# Revit family: шаблон семейства 2017
name_source: partatom
category: Датчики
revit_build: Autodesk Revit 2017 (Build: 20170118_1100(x64)
units: mm (PartAtom-declared; Revit-internal decimal feet)

## family parameters
Всегда вертикально = Нет
На основе рабочей плоскости = Нет
Общий = Нет
При загрузке вырезать с полостями = Нет
Размер круглого соединителя = Использовать диаметр
Сохранять ориентацию аннотаций = Нет
Тип детали = Нормальный
Точка расчета площади = Нет

## types (1)
- STS-103 Извещатель охранный
    ADSK_URL страницы изделия = https://stilsoft.ru
    ADSK_Единица измерения = шт.
    ADSK_Завод-изготовитель = ООО «Основа Безопасности»
    ADSK_Количество = 1
    ADSK_Марка = СТВФ.426479.056
    ADSK_Масса = 0.9
    ADSK_Наименование = Извещатель охранный STS-103
    ADSK_Размер_Высота = 95 мм
    ADSK_Размер_Длина = 165 мм
    ADSK_Размер_Ширина = 90 мм
    d_короба = 20 мм
    Видимость зоны обнаружения = Да
    Время восстановления режима готовности после срабатывания, не более, с = 10
    Время готовности после включения, не более, с = 50
    Диапазон рабочих температур, °С = -40…+50
    Диапазон регистрируемых скоростей нарушителя, м/с = от 0,1 до 5
    Длительность тревожного извещения, не менее, с = 5
    Зона обнаружения извещателя, не более, м = 50 мм
    Информационный выход = Релейный, RS-485
    Исполнение = IP65
    Исполнительное реле коммутируемое напряжение, не более, В = 72
    Исполнительное реле коммутируемый ток, не более, А = 0 А
    Напряжение электропитания постоянного тока, В = 9-30
    Наработка на ложное срабатывание, ч = 1200
    Потребляемый ток, не более, мА, при напряжении электропитания = 9В
    Потребляемый ток, не более, мА, при напряжении электропитания 12В = 0.005
    Потребляемый ток, не более, мА, при напряжении электропитания 30В = 0.003
    Потребляемый ток, не более, мА, при напряжении электропитания 9В = 0,006
    Режим работы = круглосуточный
    Устойчивость к белому свету, не менее, Лк = 20000
    Ширина/высота зоны обнаружения на дистанции 50 метров, м = 3/2
